# Revit family: ERA_LF_PR_SPO-5-40
name_source: partatom
category: Осветительные приборы
units: mm (PartAtom-declared; Revit-internal decimal feet)

## family parameters
Всегда вертикально = Да
Заголовок OmniClass = Lighting
Источник света = Да
На основе рабочей плоскости = Нет
Номер OmniClass = 23.80.70.00
Общий = Нет
При загрузке вырезать с полостями = Нет
Размер круглого соединителя = Использовать диаметр
Тип детали = Нормальный
Точка расчета площади = Да

## types (4) — shared parameters
ADSK_Единица измерения = шт.
ADSK_Завод-изготовитель = ЭРА
ADSK_Классификация нагрузок = Освещение
ADSK_Количество фаз = 1
ADSK_Коэффициент мощности = 0.9
ADSK_Наименование краткое = Светильник
ADSK_Напряжение = 230 В
ADSK_Номинальная мощность = 36 Вт
ADSK_Полная мощность = 40 В·А
ADSK_Примечание = Импульсный драйвер, поликарбонат
ADSK_Размер_Высота = 24 мм
ADSK_Размер_Длина = 1200 мм
ADSK_Размер_Ширина = 75 мм
URL = https://www.eraworld.ru
_Корпус_Высота = 24 мм
_Корпус_Диаметр = 1 мм
_Корпус_Длина = 1200 мм
_Корпус_Ширина = 75 мм
_Подвес_Диаметр = 1 мм
_Подвес_Расстояние = 1150 мм
_Подвес_Чаша_Высота = 20 мм
_Подвес_Чаша_Диаметр = 10 мм
_УГО_Диаметр = 12 мм
_УГО_Длина = 12 мм
_УГО_Ширина = 1 мм
Видимая форма излучения при визуализации = Нет
Высота чаши подвеса = 20 мм
Геометрия изделия = Прямоугольный
Диаметр подвеса = 1 мм
Диаметр чаши подвеса = 10 мм
Излучение по длине прямоугольника = 1200 мм
Излучение по ширине прямоугольника = 75 мм
Источник света = LED
Класс защиты = I
Класс пожароопасности = Нет
Комплект = Импульсный драйвер, поликарбонат
Разработчик модели = https://www.teslabim.ru
Светофильтр = 16777215
Смещение цветовой температуры при затухании лампы = <Нет>
Степень защиты IP = IP20
Тип установки = Подвесной
УГО_Масштаб = 100
Угол наклона = 90,00°
Цвет = Белый
zero-valued in all types: ADSK_Размер_Диаметр

## per-type parameters (varying)
| type | ADSK_Марка | ADSK_Масса | ADSK_Наименование | ADSK_Обозначение | Файл фотометрической сетки |
| SPO-5-40-4K-M (F), LED, IP20, 1200х75х24 мм (ДхШхВ), 36 Вт, 4000 К, 3060 лм, класс защиты I, в комплекте (импульсный драйвер, поликарбонат) | SPO-5-40-4K-M (F) | 0.46 | Светильник, LED, прямоугольный, подвесной, IP20, 1200х75х24 мм (ДхШхВ), 36 Вт, 4000 К, 3060 лм, класс защиты I, в комплекте (импульсный драйвер, поликарбонат) | SPO-5-40-4K-M (F) | SPO-5-40-4K-M (F).ies |
| SPO-5-40-6K-M (F), LED, IP20, 1200х75х24 мм (ДхШхВ), 36 Вт, 6500 К, 3060 лм, класс защиты I, в комплекте (импульсный драйвер, поликарбонат) | SPO-5-40-6K-M (F) | 0.46 | Светильник, LED, прямоугольный, подвесной, IP20, 1200х75х24 мм (ДхШхВ), 36 Вт, 6500 К, 3060 лм, класс защиты I, в комплекте (импульсный драйвер, поликарбонат) | SPO-5-40-6K-M (F) | SPO-5-40-6K-M (F).ies |
| SPO-5-40-4K-P (F), LED, IP20, 1200х75х24 мм (ДхШхВ), 36 Вт, 4000 К, 2880 лм, класс защиты I, в комплекте (импульсный драйвер, поликарбонат) | SPO-5-40-4K-P (F) | 0.42 | Светильник, LED, прямоугольный, подвесной, IP20, 1200х75х24 мм (ДхШхВ), 36 Вт, 4000 К, 2880 лм, класс защиты I, в комплекте (импульсный драйвер, поликарбонат) | SPO-5-40-4K-P (F) | SPO-5-40-4K-P (F).ies |
| SPO-5-40-6K-P (F), LED, IP20, 1200х75х24 мм (ДхШхВ), 36 Вт, 6500 К, 2880 лм, класс защиты I, в комплекте (импульсный драйвер, поликарбонат) | SPO-5-40-6K-P (F) | 0.42 | Светильник, LED, прямоугольный, подвесной, IP20, 1200х75х24 мм (ДхШхВ), 36 Вт, 6500 К, 2880 лм, класс защиты I, в комплекте (импульсный драйвер, поликарбонат) | SPO-5-40-6K-P (F) | SPO-5-40-6K-P (F).ies |
